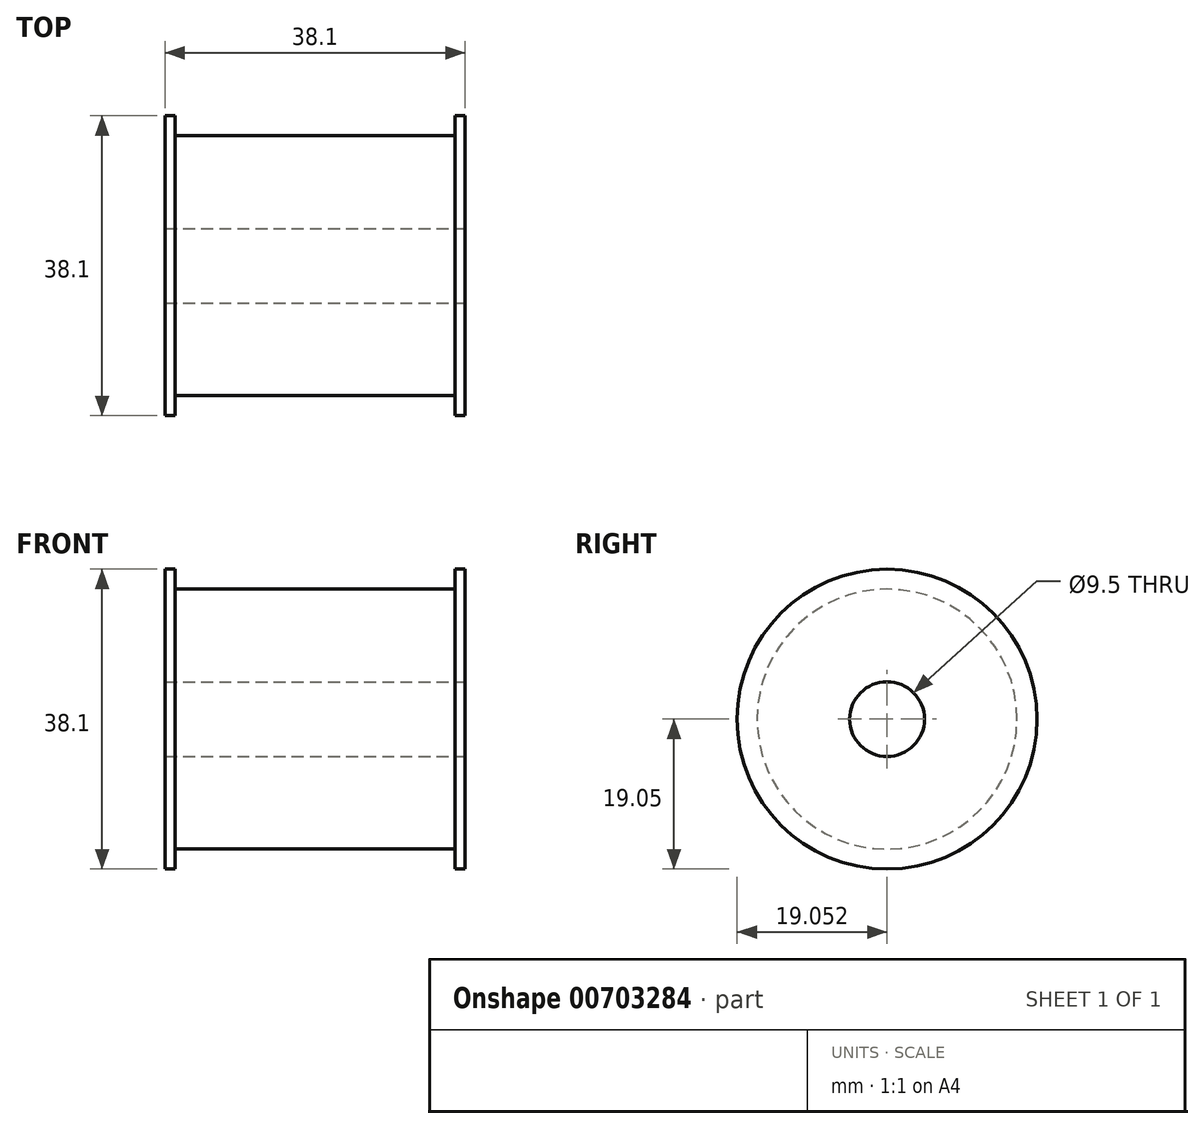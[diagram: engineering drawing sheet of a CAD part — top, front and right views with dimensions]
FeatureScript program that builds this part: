
annotation { "Feature Type Name" : "Feature", "Feature Type Description" : "" }
export const myFeature = defineFeature(function(context is Context, id is Id, definition is map)
    precondition{}
    {
        {
            var Q0;
            Q0=qCreatedBy(makeId("Top.planeOp"),FACE);
            var sketch = newSketch(context, id + "F0", { "sketchPlane" : qUnion([Q0])});
            skLineSegment(sketch, "E0.top", {"start": v(-122.08, 29.1) * mm, "end": v(-160.18, 29.1) * mm});
            skLineSegment(sketch, "E0.left", {"start": v(-160.18, 48.14) * mm, "end": v(-160.18, 29.1) * mm});
            skLineSegment(sketch, "E0.right", {"start": v(-122.08, 48.14) * mm, "end": v(-122.08, 29.1) * mm});
            skLineSegment(sketch, "E1", {"start": v(-158.91, 45.6) * mm, "end": v(-123.35, 45.6) * mm});
            skLineSegment(sketch, "E2", {"start": v(-123.35, 45.6) * mm, "end": v(-123.35, 48.14) * mm});
            skLineSegment(sketch, "E3", {"start": v(-158.91, 45.6) * mm, "end": v(-158.91, 48.14) * mm});
            skLineSegment(sketch, "E4", {"start": v(-122.08, 48.14) * mm, "end": v(-123.35, 48.14) * mm});
            skLineSegment(sketch, "E5", {"start": v(-160.18, 48.14) * mm, "end": v(-158.91, 48.14) * mm});
            skSolve(sketch);
        }
        {
            var Q0;
            Q0=makeQuery(id+"F0.imprint","IMPRINT",FACE,{"disambiguationData":[TD([[makeQuery(id+"F0.imprint","IMPRINT",EDGE,{"derivedFrom":sQuery(id+"F0.wireOp",EDGE,"E0.top")}),-1.0]])]});
            var Q1;
            Q1=sQuery(id+"F0.wireOp",EDGE,"E0.top");
            revolve(context, id + "F1", {"surfaceOperationType" : NewSurfaceOperationType.NEW, "entities" : qUnion([Q0]), "axis" : qUnion([Q1]), "revolveType" : RevolveType.FULL});
        }
        {
            var Q0;
            Q0=makeQuery(id+"F1.opRevolve","SWEPT_FACE",FACE,{"disambiguationData":[OSD([sQuery(id+"F0.wireOp",EDGE,"E0.right")])]});
            var sketch = newSketch(context, id + "F2", { "sketchPlane" : qUnion([Q0])});
            skCircle(sketch, "E6", {"center": v(29.1, 0) * mm, "radius": 4.75 * mm});
            skSolve(sketch);
        }
        {
            var Q0;
            Q0=makeQuery(id+"F2.imprint","IMPRINT",FACE,{"disambiguationData":[TD([[makeQuery(id+"F2.imprint","IMPRINT",EDGE,{"derivedFrom":sQuery(id+"F2.wireOp",EDGE,"E6")}),1.0]])]});
            extrude(context, id + "F3", {"entities" : qUnion([Q0]), "operationType" : NewBodyOperationType.REMOVE, "oppositeDirection" : true, "depth" : 38.1 * mm, "offsetDistance" : 25.4 * mm});
        }
    });
